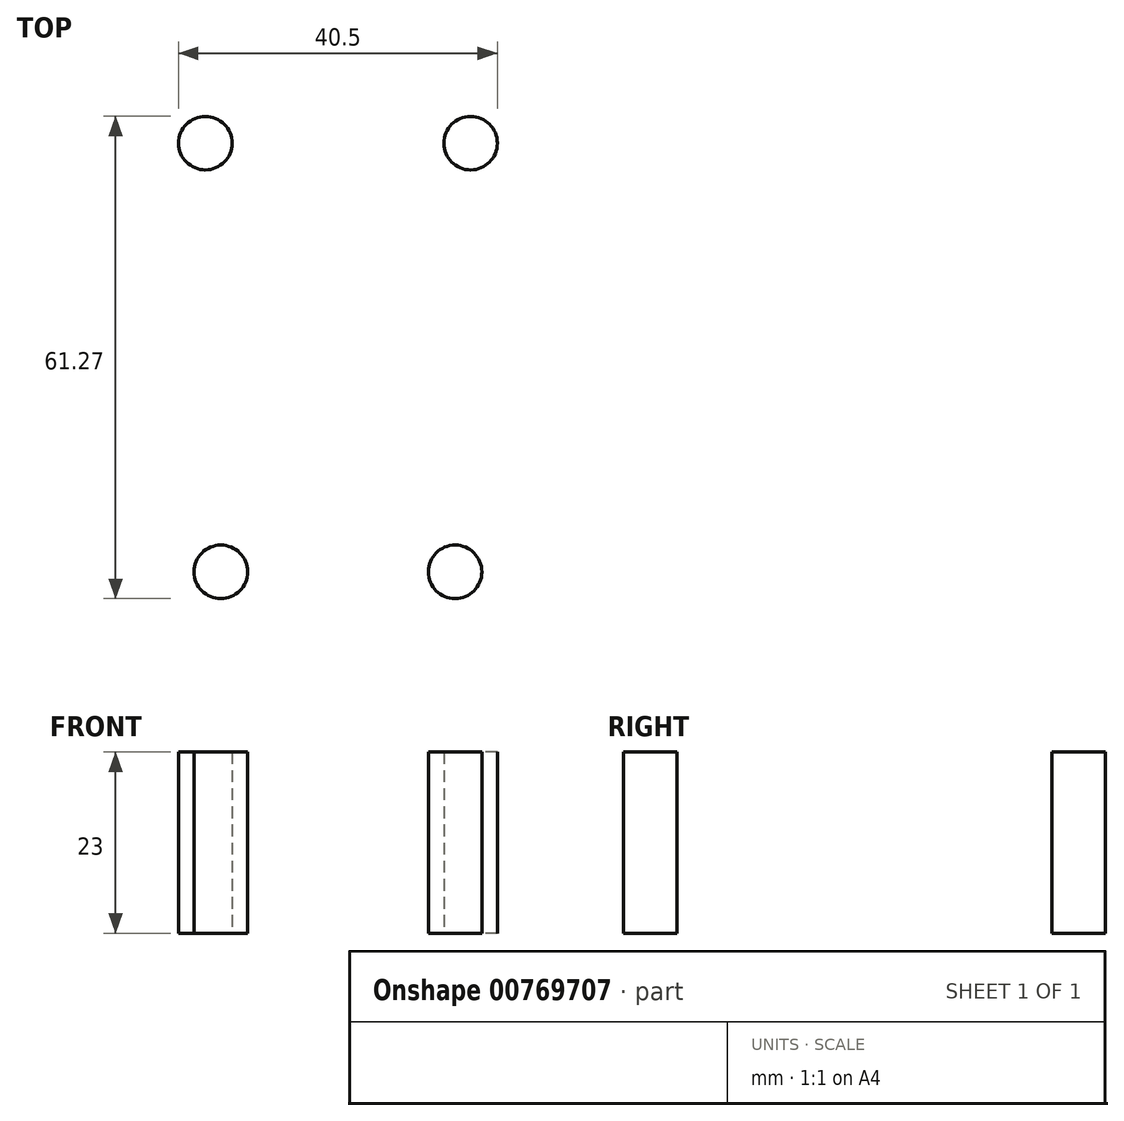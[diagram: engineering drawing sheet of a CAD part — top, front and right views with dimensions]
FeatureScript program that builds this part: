
annotation { "Feature Type Name" : "Feature", "Feature Type Description" : "" }
export const myFeature = defineFeature(function(context is Context, id is Id, definition is map)
    precondition{}
    {
        {
            var Q0;
            Q0=qCreatedBy(makeId("Top.planeOp"),FACE);
            var sketch = newSketch(context, id + "F0", { "sketchPlane" : qUnion([Q0])});
            skPoint(sketch, "E0", {"position": v(-16.85, 43.75) * mm});
            skPoint(sketch, "E1", {"position": v(16.85, 43.75) * mm});
            skPoint(sketch, "E2", {"position": v(-14.88, -10.72) * mm});
            skPoint(sketch, "E3", {"position": v(14.88, -10.72) * mm});
            skLineSegment(sketch, "E4", {"start": v(-16.85, 43.75) * mm, "end": v(16.85, 43.75) * mm, "construction": true});
            skLineSegment(sketch, "E5", {"start": v(14.88, -10.72) * mm, "end": v(-14.88, -10.72) * mm, "construction": true});
            skCircle(sketch, "E6", {"center": v(-16.85, 43.75) * mm, "radius": 1.4 * mm, "construction": true});
            skCircle(sketch, "E7", {"center": v(16.85, 43.75) * mm, "radius": 1.4 * mm, "construction": true});
            skCircle(sketch, "E8", {"center": v(14.88, -10.72) * mm, "radius": 1.4 * mm, "construction": true});
            skCircle(sketch, "E9", {"center": v(-14.88, -10.72) * mm, "radius": 1.4 * mm, "construction": true});
            skCircle(sketch, "E10.0", {"center": v(-16.85, 43.75) * mm, "radius": 3.4 * mm});
            skCircle(sketch, "E11.0", {"center": v(16.85, 43.75) * mm, "radius": 3.4 * mm});
            skCircle(sketch, "E12.0", {"center": v(-14.88, -10.72) * mm, "radius": 3.4 * mm});
            skCircle(sketch, "E13.0", {"center": v(14.88, -10.72) * mm, "radius": 3.4 * mm});
            skSolve(sketch);
        }
        {
            var Q0;
            Q0=makeQuery(id+"F0.imprint","IMPRINT",FACE,{"disambiguationData":[TD([[makeQuery(id+"F0.imprint","IMPRINT",EDGE,{"derivedFrom":sQuery(id+"F0.wireOp",EDGE,"E10.0")}),1.0]])]});
            var Q1;
            Q1=makeQuery(id+"F0.imprint","IMPRINT",FACE,{"disambiguationData":[TD([[makeQuery(id+"F0.imprint","IMPRINT",EDGE,{"derivedFrom":sQuery(id+"F0.wireOp",EDGE,"E11.0")}),1.0]])]});
            var Q2;
            Q2=makeQuery(id+"F0.imprint","IMPRINT",FACE,{"disambiguationData":[TD([[makeQuery(id+"F0.imprint","IMPRINT",EDGE,{"derivedFrom":sQuery(id+"F0.wireOp",EDGE,"E13.0")}),1.0]])]});
            var Q3;
            Q3=makeQuery(id+"F0.imprint","IMPRINT",FACE,{"disambiguationData":[TD([[makeQuery(id+"F0.imprint","IMPRINT",EDGE,{"derivedFrom":sQuery(id+"F0.wireOp",EDGE,"E12.0")}),1.0]])]});
            var Q4;
            Q4=sQuery(id+"F0.wireOp",EDGE,"E12.0");
            var Q5;
            Q5=sQuery(id+"F0.wireOp",EDGE,"E10.0");
            var Q6;
            Q6=sQuery(id+"F0.wireOp",EDGE,"E11.0");
            var Q7;
            Q7=sQuery(id+"F0.wireOp",EDGE,"E13.0");
            extrude(context, id + "F1", {"entities" : qUnion([Q0, Q1, Q2, Q3]), "surfaceEntities" : qUnion([Q4, Q5, Q6, Q7]), "depth" : 23 * mm, "offsetDistance" : 25 * mm});
        }
    });
